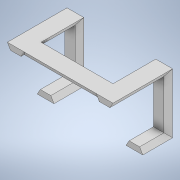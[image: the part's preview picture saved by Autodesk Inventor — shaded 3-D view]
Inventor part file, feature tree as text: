
AUTODESK INVENTOR PART (.ipt)
format: ipt  version: 2020 (Build 240168000, 168)  size: 184,832 bytes
history: native  units: mm
features: extrude x4, sketch x4, projected_geometry x2
ambient origin geometry x8: Origin, YZ Plane, XZ Plane, XY Plane, X Axis, Y Axis, Z Axis, Center Point
bodies: Solid1 (feature_tree)
feature tree (10):
  extrude  "Extrusion1"  Depth=8.990381mm
  extrude  "Extrusion2"  Depth=32.412535mm
  extrude  "Extrusion3"  Depth=4.0mm
  extrude  "Extrusion4"  Depth=21.752405mm
  sketch  "Sketch1"  dims[d0=118.0mm d1=8.990381mm]
  sketch  "Sketch2"  dims[d2=40.0mm d4=32.412535mm]
  sketch  "Sketch3"  dims[d5=10.0mm d7=10.0mm d9=4.0mm]
  sketch  "Sketch6"  dims[d10=2.0mm d11=2.0mm d12=4.0mm d13=43.618802mm d14=0.0mm d15=4.0mm d16=43.504809mm d17=0.0mm d18=7.650139mm d20=12.268941mm d21=12.268941mm d22=7.650139mm d23=38.547mm d24=0.0mm d25=21.752405mm d26=0.0mm d27=0.5mm d28=0.872665mm]
  projected_geometry  "Projected Loop4"
  projected_geometry  "Projected Loop5"
